# Revit family: Recessed_Inground_Cooper_Lumiere_Boca_696
name_source: partatom
category: Lighting Fixtures
revit_build: Autodesk Revit 2014 (Build: 20131024_2115(x64)
units: mm (PartAtom-declared; Revit-internal decimal feet)

## types (2) — shared parameters
Assembly Code = D5020
Ballast Type = Ballast
Bulb Biaxial Angle = 0.00°
Default Elevation = 0' - 0"
Diffuser Material = Glass - Cooper Industries - Clear
Emit Shape Visible in Rendering = No
Frame Material = Metal - Cooper Industries - Steel - White
Has Biaxial Bulb = No
Housing Type = Stainless steel recessed housing
Lamp = LED
Lamp Quantity = 1
Light Bulb Material = Glass - Cooper Industries - Clear
Load Classificattion = L
Model = 696
No of Circuits = 1
Number of Poles = 1
Options = Options : Peach Dichroic Filter, 2.00” Dia
Packaging = Unit Pack
Product Documentation Link = http://www.cooperindustries.com
Product Page URL = http://www.cooperindustries.com
Series = Boca
Shipping Weight = 0 lb
URL = http://www.cooperlighting.com
Voltage = 277
Wattage Comments = 12
Wiring Access Diameter = 0' - 0"
zero-valued in all types: Ballast Quantity, Power Factor

## per-type parameters (varying)
| type | Apparent Load | Ballast Voltage | Description | Manufacturer | Supply Voltage | Total Input Wattage |
| 6 1/4"D-1Lamp-12W-LED-120V | 34 VA | 277 V | EXTERIOR INGRADE LED SIGN FLOOD LIGHT | HYDREL LIGHTING | 277 V | 34 W |
| Tree Uplight | 12 VA | 120 V | EXTERIOR INGRADE LED TREE UPLIGHT | WINONA | 120 V | 12 W |

## geometry (parser evidence)
native form markers: Sweep x20
no freeform markers — native parametric forms only
